# Revit family: 15. Plumbing_Fixtures_Grohe_Allure_Brilliant_Concealed_23200000_14_METRIC
name_source: partatom
category: Plumbing Fixtures
revit_build: Autodesk Revit 2014 (Build: 20130308_1515(x64)
units: mm (PartAtom-declared; Revit-internal decimal feet)

## types (2) — shared parameters
ADA Compliant = Yes
Assembly Code = C1030220
AssetType = Fixed
Base Material = Plastic, Opaque Black
Brass = Brass
CW Connection = No
ClassificationName = Uniclass2015
ClassificationValue = Pr_40_20_87_75
Cold Water Connection Diameter = 10 mm  [stored 0.0328084 ft]
Color = Chrome
Default Elevation = 600 mm
Description = Allure Brilliant Single lever mixer 1/2 concealed body
DocumentationMaintenance = https://specifi.bimstore.co.uk
DocumentationTechnical = https://specifi.bimstore.co.uk
DurationUnit = Years
Ecojoy = No
Finish = Chrome
HW Connection = No
Height = 210 mm  [stored 0.688976 ft]
Hot Water Connection Diameter = 10 mm  [stored 0.0328084 ft]
Keynote = N13
Length = 197 mm
Low Emitting Material = No
Manufacturer = Grohe AG
Material = Chrome
Model = Allure Brilliant Single Lever Mixer - 23200000
ModelNumber = 23200000
NBSDescription = Shower fittings package
NBSObjectName = Shower fittings package
NBSReference = 45-35-70/330
Name = Allure Brilliant Single Lever Mixer - 23200000
Offset from wall = 50 mm  [stored 0.164042 ft]
P Length = 40 mm  [stored 0.131234 ft]
Plastic = Plastic, Formed
Plate Width = 173 mm  [stored 0.567585 ft]
Product Page URL = http://www.grohe.co.uk
ProductionYear = 2015
Spare Parts List = http://www.grohe.co.uk
Type Comments = Allure Brilliant Single lever mixer 1/2 concealed body
TypeName = Allure Brilliant Single lever mixer 1/2 concealed body
URL = www.grohe.com
Vent Connection = No
WarrantyDurationUnit = Years
Waste Connection = No
Width = 129 mm  [stored 0.423228 ft]
_current revision = 1
_distributed by = www.bimstore.co.uk
p Rad = 10 mm  [stored 0.0328084 ft]
zero-valued in all types: CWFU, Cost, ExpectedLife, HWFU, Percentage of Recycled Content, WFU, _BIMspec_GUID

## per-type parameters (varying)
| type | 45 | 75 | Adjustable Depth | Size |
| Depth - 75mm | No | Yes | 75 mm | 75mm |
| Depth - 45mm | Yes | No | 45 mm  [stored 0.147638 ft] | 45mm |

note: [stored X ft] marks values corroborated as IEEE doubles in the binary element streams (Revit-internal decimal feet)

## geometry (parser evidence)
native form markers: Blend x10, Sweep x1
no freeform markers — native parametric forms only
